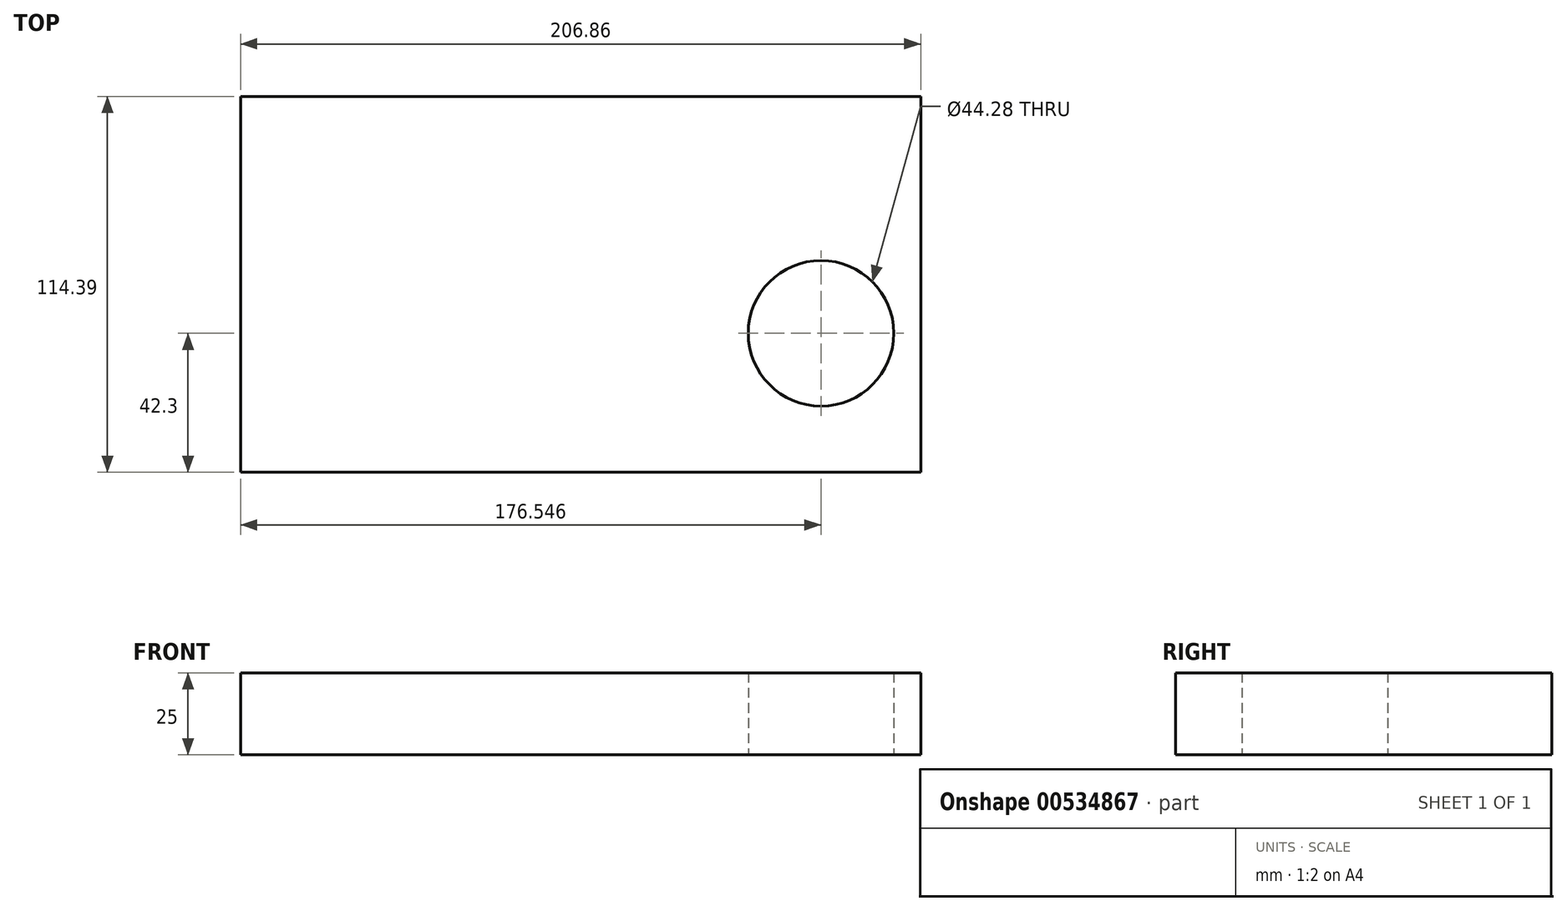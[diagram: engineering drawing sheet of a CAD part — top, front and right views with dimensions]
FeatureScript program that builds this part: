
annotation { "Feature Type Name" : "Feature", "Feature Type Description" : "" }
export const myFeature = defineFeature(function(context is Context, id is Id, definition is map)
    precondition{}
    {
        {
            var Q0;
            Q0=qCreatedBy(makeId("Top.planeOp"),FACE);
            var sketch = newSketch(context, id + "F0", { "sketchPlane" : qUnion([Q0])});
            skLineSegment(sketch, "E0.bottom", {"start": v(164.99, 71.75) * mm, "end": v(-41.87, 71.75) * mm});
            skLineSegment(sketch, "E0.top", {"start": v(164.99, -42.64) * mm, "end": v(-41.87, -42.64) * mm});
            skLineSegment(sketch, "E0.left", {"start": v(164.99, 71.75) * mm, "end": v(164.99, -42.64) * mm});
            skLineSegment(sketch, "E0.right", {"start": v(-41.87, 71.75) * mm, "end": v(-41.87, -42.64) * mm});
            skCircle(sketch, "E1", {"center": v(134.68, -0.34) * mm, "radius": 22.14 * mm});
            skSolve(sketch);
        }
        {
            var Q0;
            Q0=qSketchRegion(id+"F0",true);
            extrude(context, id + "F1", {"entities" : qUnion([Q0]), "depth" : 25 * mm, "offsetDistance" : 25 * mm});
        }
    });
